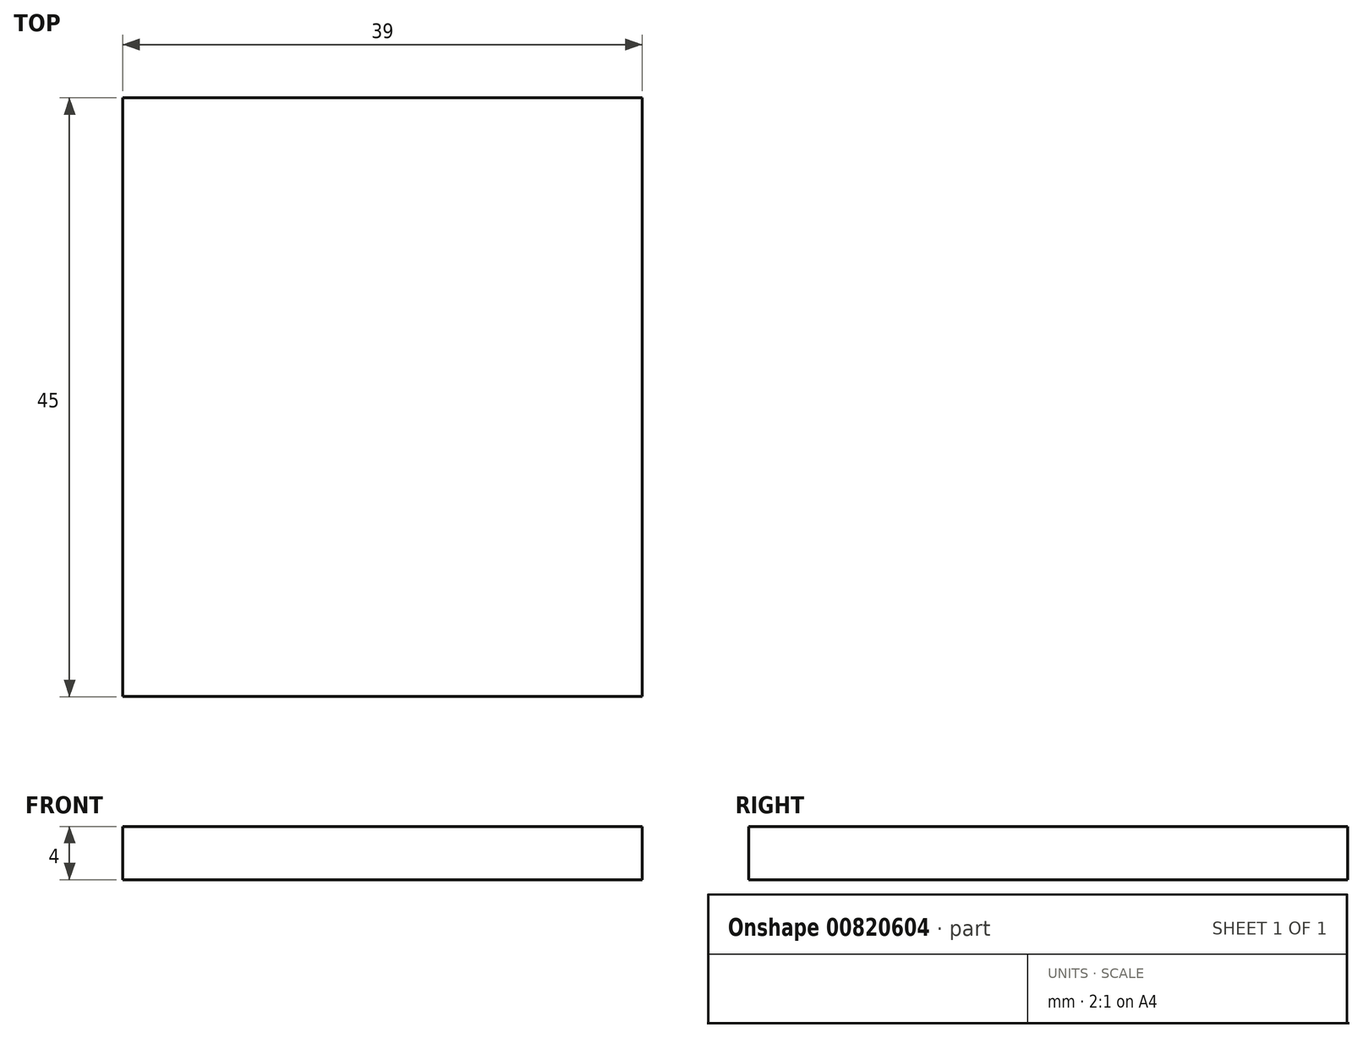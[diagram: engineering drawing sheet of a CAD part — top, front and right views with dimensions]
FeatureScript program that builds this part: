
annotation { "Feature Type Name" : "Feature", "Feature Type Description" : "" }
export const myFeature = defineFeature(function(context is Context, id is Id, definition is map)
    precondition{}
    {
        {
            var Q0;
            Q0=qCreatedBy(makeId("Top.planeOp"),FACE);
            var sketch = newSketch(context, id + "F0", { "sketchPlane" : qUnion([Q0])});
            skLineSegment(sketch, "E0.bottom", {"start": v(-21.15, 28.25) * mm, "end": v(17.85, 28.25) * mm});
            skLineSegment(sketch, "E0.top", {"start": v(-21.15, -16.75) * mm, "end": v(17.85, -16.75) * mm});
            skLineSegment(sketch, "E0.left", {"start": v(-21.15, 28.25) * mm, "end": v(-21.15, -16.75) * mm});
            skLineSegment(sketch, "E0.right", {"start": v(17.85, 28.25) * mm, "end": v(17.85, -16.75) * mm});
            skSolve(sketch);
        }
        {
            var Q0;
            Q0=qSketchRegion(id+"F0",true);
            extrude(context, id + "F1", {"entities" : qUnion([Q0]), "depth" : 4 * mm, "offsetDistance" : 25 * mm});
        }
    });
